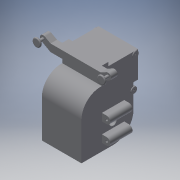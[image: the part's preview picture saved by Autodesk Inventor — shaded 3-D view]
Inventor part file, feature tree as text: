
AUTODESK INVENTOR PART (.ipt)
format: ipt  version: 2019 (Build 230136000, 136)  size: 266,752 bytes
history: native  units: in
note: dims shown in document units (in); Inventor stores cm internally (conversion verified against a paired STEP export)
features: sketch x12, extrude x11, mirror x2, hole x1, fillet x1
ambient origin geometry x8: Origin, YZ Plane, XZ Plane, XY Plane, X Axis, Y Axis, Z Axis, Center Point
bodies: Solid1 (feature_tree)
feature tree (27):
  extrude  "Extrusion1"  Depth=2.2in
  extrude  "Extrusion2"  Depth=3.8in
  extrude  "Extrusion3"  Depth=0.75in
  extrude  "Extrusion4"  Depth=0.4in
  extrude  "Extrusion5"  Depth=0.2in
  extrude  "Extrusion9"  Depth=0.35in TaperAngle=0.0deg
  extrude  "Extrusion10"  Depth=0.35in
  hole  "Hole1"  [1 undecoded]
  extrude  "Extrusion6"  Depth=0.4in TaperAngle=0.0deg
  extrude  "Extrusion7"  Depth=0.25in
  mirror  "Mirror1"
  extrude  "Extrusion11"  Depth=1.2in TaperAngle=0.0deg
  extrude  "Extrusion12"  Depth=1.2in TaperAngle=0.0deg
  fillet  "Fillet1"  Radius=0.32in
  mirror  "Mirror2"
  sketch  "Sketch2"  dims[d0=2.2in d1=2.06in]
  sketch  "Sketch3"  dims[d2=1.7in d3=3.8in]
  sketch  "Sketch4"  dims[d4=2.8in d5=0.75in]
  sketch  "Sketch6"  dims[d6=2.13in d7=0.0in d8=0.4in]
  sketch  "Sketch7"  dims[d9=2.7in d10=0.2in]
  sketch  "Sketch8"  dims[d11=0.35in d12=0.0in d13=0.35in d14=0.0in]
  sketch  "Sketch9"  dims[d17=0.35in d19=0.35in]
  sketch  "Sketch11"  dims[d20=0.15in d21=0.35in d22=0.0in]
  sketch  "Sketch12"  dims[d23=0.4in d24=0.4in d25=0.0in]
  sketch  "Sketch13"  dims[d26=0.4in d27=0.25in]
  sketch  "Sketch15"  dims[d28=0.5in d29=1.2in d30=0.0in]
  sketch  "Sketch16"  dims[d31=0.125in d32=1.2in d33=0.0in d34=0.32in d35=0.25in d36=1.42in d39=1.2in d40=0.0in d41=2.2in d42=0.0in d43=0.076in d44=0.95in d45=0.225in d46=0.125in d47=0.5635in d48=1.0in d49=0.8108in d50=0.55in d51=0.0in d52=0.15in d53=0.1in d54=0.0in]
note: 1 required parameter value undecoded (feature->parameter linkage not recoverable at this tier; creation-order binding heuristic only, values carry confidence <= 0.55)
